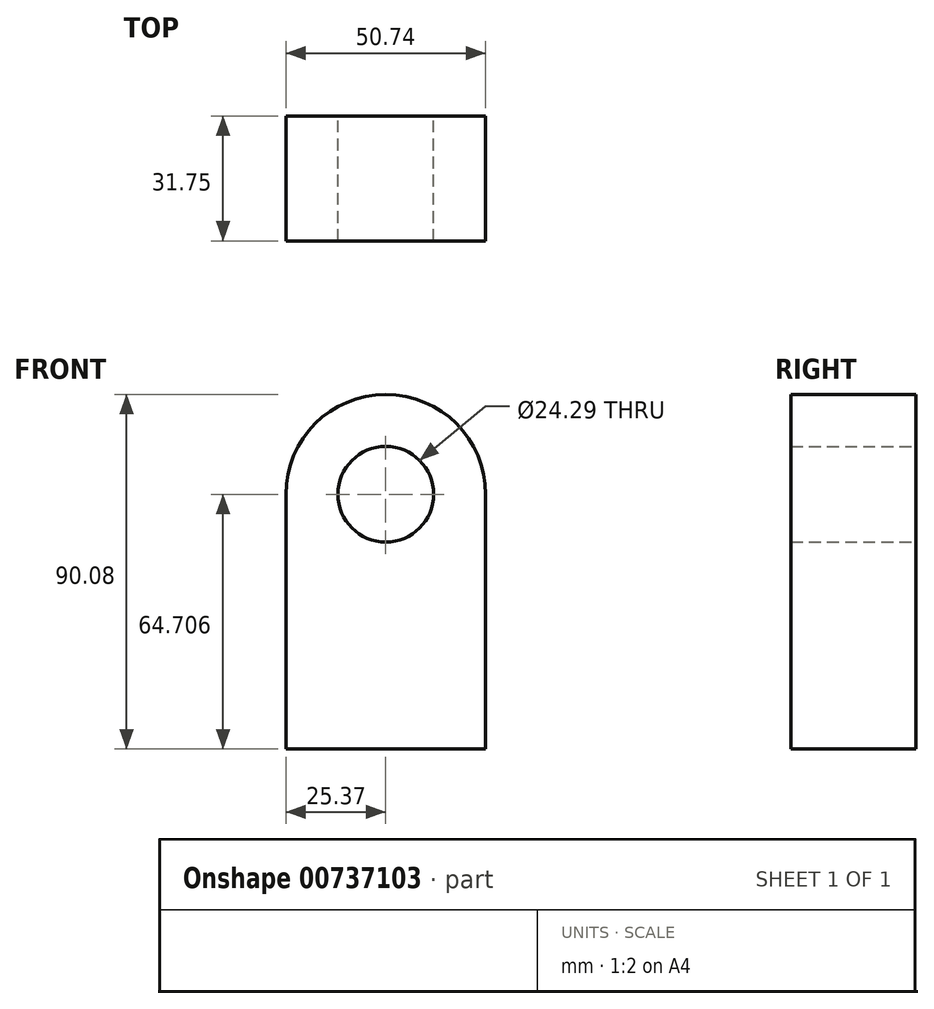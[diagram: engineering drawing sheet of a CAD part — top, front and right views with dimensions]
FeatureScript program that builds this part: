
annotation { "Feature Type Name" : "Feature", "Feature Type Description" : "" }
export const myFeature = defineFeature(function(context is Context, id is Id, definition is map)
    precondition{}
    {
        {
            var Q0;
            Q0=qCreatedBy(makeId("Front.planeOp"),FACE);
            var sketch = newSketch(context, id + "F0", { "sketchPlane" : qUnion([Q0])});
            skLineSegment(sketch, "E0", {"start": v(-25.37, 19.47) * mm, "end": v(-25.37, -45.24) * mm});
            skLineSegment(sketch, "E1", {"start": v(-25.37, -45.24) * mm, "end": v(25.37, -45.24) * mm});
            skLineSegment(sketch, "E2", {"start": v(25.37, -45.24) * mm, "end": v(25.37, 19.47) * mm});
            skArc(sketch, "E3", {"start": v(25.37, 19.47) * mm, "mid": v(0, 44.84) * mm, "end": v(-25.37, 19.47) * mm});
            skCircle(sketch, "E4", {"center": v(0, 19.47) * mm, "radius": 12.15 * mm});
            skPoint(sketch, "E5.end.orphan", {"position": v(-25.37, 19.47) * mm});
            skSolve(sketch);
        }
        {
            var Q0;
            Q0=makeQuery(id+"F0.imprint","IMPRINT",FACE,{"disambiguationData":[TD([[makeQuery(id+"F0.imprint","IMPRINT",EDGE,{"derivedFrom":sQuery(id+"F0.wireOp",EDGE,"E0")}),1.0]])]});
            extrude(context, id + "F1", {"entities" : qUnion([Q0]), "depth" : 31.75 * mm, "offsetDistance" : 25.4 * mm});
        }
    });
